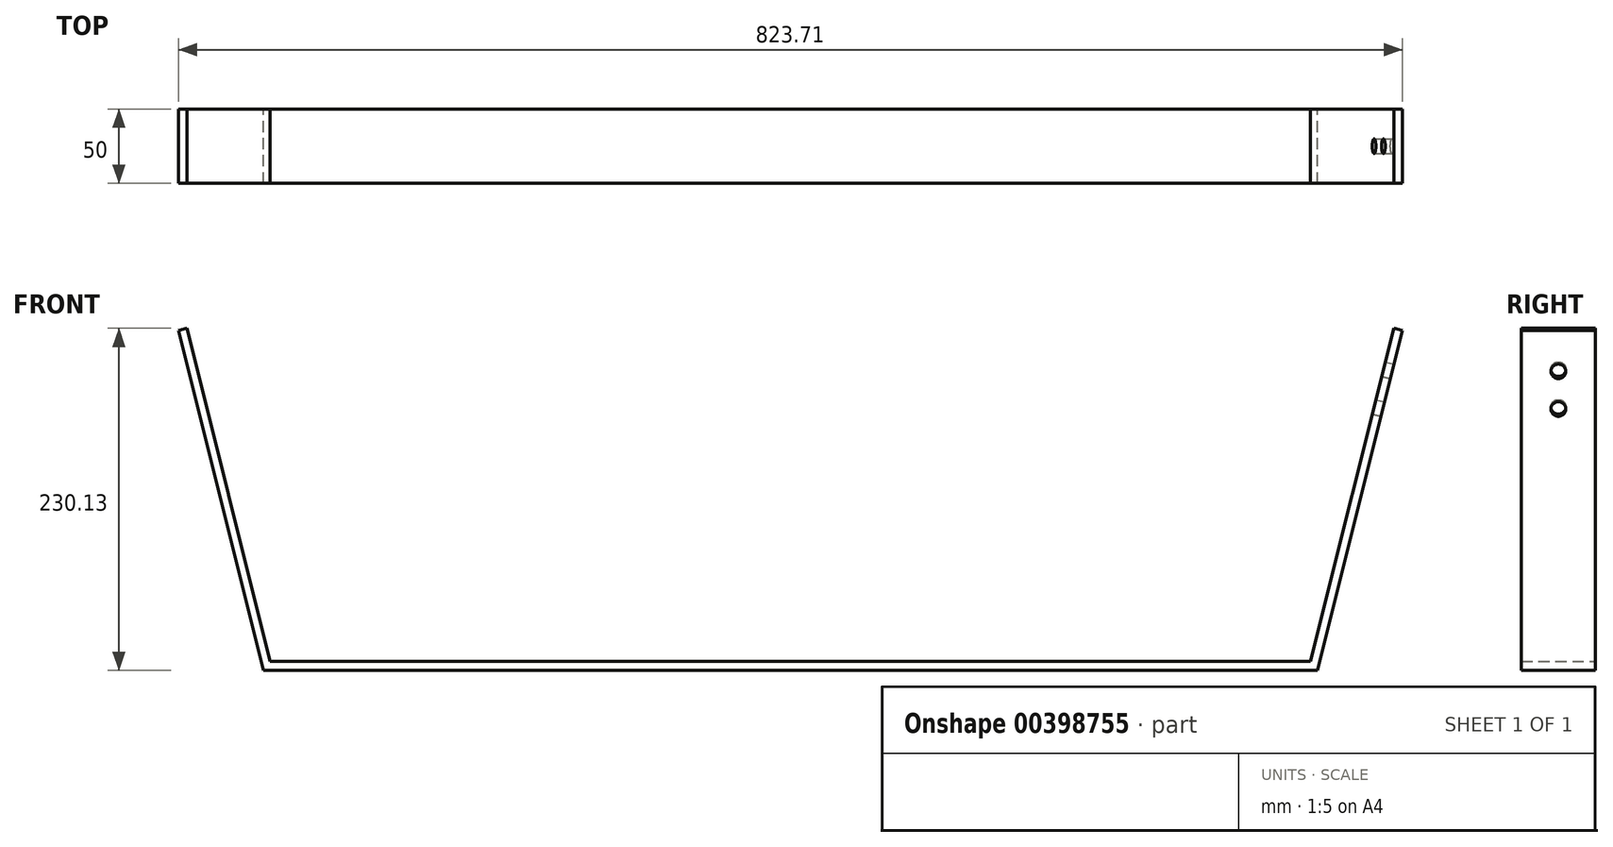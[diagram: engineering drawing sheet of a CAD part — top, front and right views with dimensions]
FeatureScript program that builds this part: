
annotation { "Feature Type Name" : "Feature", "Feature Type Description" : "" }
export const myFeature = defineFeature(function(context is Context, id is Id, definition is map)
    precondition{}
    {
        {
            var Q0;
            Q0=qCreatedBy(makeId("Front.planeOp"),FACE);
            var sketch = newSketch(context, id + "F0", { "sketchPlane" : qUnion([Q0])});
            skLineSegment(sketch, "E0", {"start": v(-364.85, -59.52) * mm, "end": v(335.15, -59.52) * mm});
            skLineSegment(sketch, "E1", {"start": v(-364.85, -59.52) * mm, "end": v(-408.6, 115.5) * mm});
            skLineSegment(sketch, "E2", {"start": v(335.15, -59.52) * mm, "end": v(378.9, 115.5) * mm});
            skLineSegment(sketch, "E3", {"start": v(-364.85, -59.52) * mm, "end": v(-420.88, 164.61) * mm});
            skLineSegment(sketch, "E4", {"start": v(335.15, -59.52) * mm, "end": v(391.19, 164.61) * mm});
            skLineSegment(sketch, "E5", {"start": v(-420.88, 164.61) * mm, "end": v(-426.7, 163.16) * mm});
            skLineSegment(sketch, "E6", {"start": v(-426.7, 163.16) * mm, "end": v(-369.53, -65.52) * mm});
            skLineSegment(sketch, "E7", {"start": v(-142.27, -59.52) * mm, "end": v(-142.27, -65.52) * mm});
            skLineSegment(sketch, "E8", {"start": v(-142.27, -65.52) * mm, "end": v(-369.53, -65.52) * mm});
            skLineSegment(sketch, "E9", {"start": v(-142.27, -65.52) * mm, "end": v(339.84, -65.52) * mm});
            skLineSegment(sketch, "E10", {"start": v(391.19, 164.61) * mm, "end": v(397, 163.16) * mm});
            skLineSegment(sketch, "E11", {"start": v(397, 163.16) * mm, "end": v(339.84, -65.52) * mm});
            skSolve(sketch);
        }
        {
            var Q0;
            {var subQ0=sQuery(id+"F0.wireOp",EDGE,"E5");Q0=makeQuery(id+"F0.imprint","IMPRINT",FACE,{"disambiguationData":[TD([[makeQuery(id+"F0.imprint","IMPRINT",EDGE,{"derivedFrom":subQ0}),1.0]])]});}
            var Q1;
            {var subQ4=sQuery(id+"F0.wireOp",EDGE,"E7");Q1=makeQuery(id+"F0.imprint","IMPRINT",FACE,{"disambiguationData":[TD([[makeQuery(id+"F0.imprint","IMPRINT",EDGE,{"derivedFrom":subQ4}),1.0]])]});}
            extrude(context, id + "F1", {"entities" : qUnion([Q0, Q1]), "depth" : 50 * mm});
        }
        {
            var Q0;
            Q0=makeQuery(id+"F1.opExtrude","SWEPT_FACE",FACE,{"disambiguationData":[OSD([sQuery(id+"F0.wireOp",EDGE,"E11")])]});
            var sketch = newSketch(context, id + "F2", { "sketchPlane" : qUnion([Q0])});
            skCircle(sketch, "E12", {"center": v(-25, 226.21) * mm, "radius": 5 * mm});
            skPoint(sketch, "E13.start.orphan", {"position": v(-50, 197.85) * mm});
            skPoint(sketch, "E14.trimOffspring.end.orphan", {"position": v(0, 254.57) * mm});
            skCircle(sketch, "E15", {"center": v(-25, 200.1) * mm, "radius": 5 * mm});
            skSolve(sketch);
        }
        {
            var Q0;
            Q0=makeQuery(id+"F2.imprint","IMPRINT",FACE,{"disambiguationData":[TD([[makeQuery(id+"F2.imprint","IMPRINT",EDGE,{"derivedFrom":sQuery(id+"F2.wireOp",EDGE,"E12")}),1.0]])]});
            var Q1;
            Q1=makeQuery(id+"F2.imprint","IMPRINT",FACE,{"disambiguationData":[TD([[makeQuery(id+"F2.imprint","IMPRINT",EDGE,{"derivedFrom":sQuery(id+"F2.wireOp",EDGE,"E15")}),1.0]])]});
            extrude(context, id + "F3", {"entities" : qUnion([Q0, Q1]), "operationType" : NewBodyOperationType.REMOVE, "oppositeDirection" : true, "depth" : 149 * mm});
        }
    });
